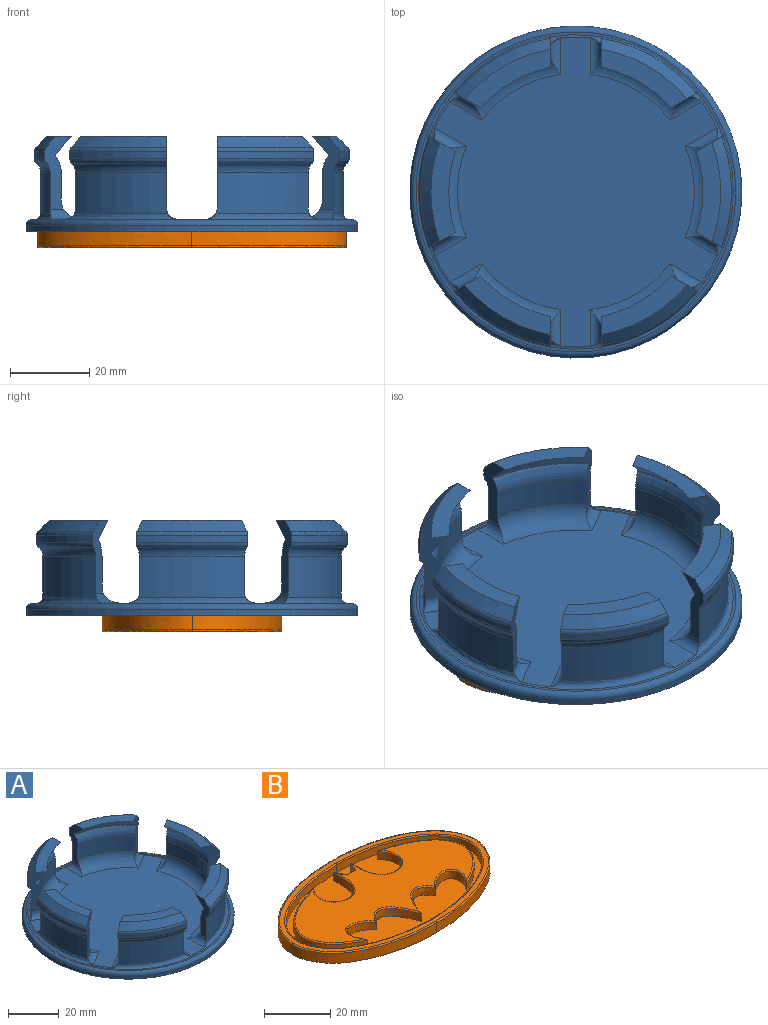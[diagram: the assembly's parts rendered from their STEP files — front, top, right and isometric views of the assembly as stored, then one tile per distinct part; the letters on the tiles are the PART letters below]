
ASSEMBLY  parts=2 mates=1
PART A: 102 faces, bbox 90.7x90.7x24.1 mm
  f0: cylinder r=38.1mm len=27.08mm, axis (0,0,-1), area 280.7mm2, adj f3,f66,f94,f96,f99,f101
  f1: cylinder r=39.69mm len=28.18mm, axis (0,0,-1), area 51mm2, adj f5,f6,f94,f99
  f2: plane 24.96x6.16mm, normal (0,0,1), area 103.8mm2, adj f4,f10,f94,f99
  f3: torus R=41.27mm, axis (0,0,1), area 74.2mm2, adj f0,f6,f94,f99
  f4: cone r=36.51mm half-angle=45deg, axis (0,0,-1), area 103.8mm2, adj f2,f5,f94,f99
  f5: torus R=38.16mm, axis (0,0,1), area 34.3mm2, adj f1,f4,f94,f99
  f6: torus R=38.16mm, axis (0,0,-1), area 36.9mm2, adj f1,f3,f94,f99
  f7: cylinder r=34.92mm len=23.34mm, axis (0,0,-1), area 158.2mm2, adj f9,f11,f94,f99
  f8: cylinder r=36.51mm len=24.96mm, axis (0,0,-1), area 10.4mm2, adj f9,f10,f94,f99
  f9: torus R=41.27mm, axis (0,0,1), area 112.2mm2, adj f7,f8,f94,f99
  f10: cone r=34.27mm half-angle=45deg, axis (0,0,-1), area 146.5mm2, adj f2,f8,f94,f99
  f11: torus R=29.84mm, axis (0,0,1), area 184.7mm2, adj f7,f72,f94,f96,f99,f101
  f12: cylinder r=38.1mm len=23.46mm, axis (0,0,-1), area 280.7mm2, adj f15,f66,f90,f92,f95,f97
  f13: cylinder r=39.69mm len=24.4mm, axis (0,0,-1), area 51mm2, adj f17,f18,f90,f95
  f14: plane 21.61x14.76mm, normal (0,0,1), area 103.8mm2, adj f16,f22,f90,f95
  f15: torus R=41.27mm, axis (0,0,1), area 74.2mm2, adj f12,f18,f90,f95
  f16: cone r=36.51mm half-angle=45deg, axis (0,0,-1), area 103.8mm2, adj f14,f17,f90,f95
  f17: torus R=38.16mm, axis (0,0,1), area 34.3mm2, adj f13,f16,f90,f95
  f18: torus R=38.16mm, axis (0,0,-1), area 36.9mm2, adj f13,f15,f90,f95
  f19: cylinder r=34.92mm len=20.22mm, axis (0,0,-1), area 158.2mm2, adj f21,f23,f90,f95
  f20: cylinder r=36.51mm len=21.61mm, axis (0,0,-1), area 10.4mm2, adj f21,f22,f90,f95
  f21: torus R=41.27mm, axis (0,0,1), area 112.2mm2, adj f19,f20,f90,f95
  f22: cone r=34.27mm half-angle=45deg, axis (0,0,-1), area 146.5mm2, adj f14,f20,f90,f95
  f23: torus R=29.84mm, axis (0,0,1), area 184.7mm2, adj f19,f72,f90,f92,f95,f97
  f24: cylinder r=38.1mm len=23.46mm, axis (0,0,-1), area 280.7mm2, adj f27,f66,f86,f88,f91,f93
  f25: cylinder r=39.69mm len=24.4mm, axis (0,0,-1), area 51mm2, adj f29,f30,f86,f91
  f26: plane 21.61x14.76mm, normal (0,0,1), area 103.8mm2, adj f28,f34,f86,f91
  f27: torus R=41.27mm, axis (0,0,1), area 74.2mm2, adj f24,f30,f86,f91
  f28: cone r=36.51mm half-angle=45deg, axis (0,0,-1), area 103.8mm2, adj f26,f29,f86,f91
  f29: torus R=38.16mm, axis (0,0,1), area 34.3mm2, adj f25,f28,f86,f91
  f30: torus R=38.16mm, axis (0,0,-1), area 36.9mm2, adj f25,f27,f86,f91
  f31: cylinder r=34.92mm len=20.22mm, axis (0,0,-1), area 158.2mm2, adj f33,f35,f86,f91
  f32: cylinder r=36.51mm len=21.61mm, axis (0,0,-1), area 10.4mm2, adj f33,f34,f86,f91
  f33: torus R=41.27mm, axis (0,0,1), area 112.2mm2, adj f31,f32,f86,f91
  f34: cone r=34.27mm half-angle=45deg, axis (0,0,-1), area 146.5mm2, adj f26,f32,f86,f91
  f35: torus R=29.84mm, axis (0,0,1), area 184.7mm2, adj f31,f72,f86,f88,f91,f93
  f36: cylinder r=38.1mm len=27.08mm, axis (0,0,-1), area 280.7mm2, adj f39,f66,f82,f84,f87,f89
  f37: cylinder r=39.69mm len=28.18mm, axis (0,0,-1), area 51mm2, adj f41,f42,f82,f87
  f38: plane 24.96x6.16mm, normal (0,0,1), area 103.8mm2, adj f40,f46,f82,f87
  f39: torus R=41.27mm, axis (0,0,1), area 74.2mm2, adj f36,f42,f82,f87
  f40: cone r=36.51mm half-angle=45deg, axis (0,0,-1), area 103.8mm2, adj f38,f41,f82,f87
  f41: torus R=38.16mm, axis (0,0,1), area 34.3mm2, adj f37,f40,f82,f87
  f42: torus R=38.16mm, axis (0,0,-1), area 36.9mm2, adj f37,f39,f82,f87
  f43: cylinder r=34.92mm len=23.34mm, axis (0,0,-1), area 158.2mm2, adj f45,f47,f82,f87
  f44: cylinder r=36.51mm len=24.96mm, axis (0,0,-1), area 10.4mm2, adj f45,f46,f82,f87
  f45: torus R=41.27mm, axis (0,0,1), area 112.2mm2, adj f43,f44,f82,f87
  f46: cone r=34.27mm half-angle=45deg, axis (0,0,-1), area 146.5mm2, adj f38,f44,f82,f87
  f47: torus R=29.84mm, axis (0,0,1), area 184.7mm2, adj f43,f72,f82,f84,f87,f89
  f48: cylinder r=38.1mm len=23.46mm, axis (0,0,-1), area 280.7mm2, adj f51,f66,f78,f80,f83,f85
  f49: cylinder r=39.69mm len=24.4mm, axis (0,0,-1), area 51mm2, adj f53,f54,f78,f83
  f50: plane 21.61x14.76mm, normal (0,0,1), area 103.8mm2, adj f52,f58,f78,f83
  f51: torus R=41.27mm, axis (0,0,1), area 74.2mm2, adj f48,f54,f78,f83
  f52: cone r=36.51mm half-angle=45deg, axis (0,0,-1), area 103.8mm2, adj f50,f53,f78,f83
  f53: torus R=38.16mm, axis (0,0,1), area 34.3mm2, adj f49,f52,f78,f83
  f54: torus R=38.16mm, axis (0,0,-1), area 36.9mm2, adj f49,f51,f78,f83
  f55: cylinder r=34.92mm len=20.22mm, axis (0,0,-1), area 158.2mm2, adj f57,f59,f78,f83
  f56: cylinder r=36.51mm len=21.61mm, axis (0,0,-1), area 10.4mm2, adj f57,f58,f78,f83
  f57: torus R=41.27mm, axis (0,0,1), area 112.2mm2, adj f55,f56,f78,f83
  f58: cone r=34.27mm half-angle=45deg, axis (0,0,-1), area 146.5mm2, adj f50,f56,f78,f83
  f59: torus R=29.84mm, axis (0,0,1), area 184.7mm2, adj f55,f72,f78,f80,f83,f85
  f60: cylinder r=41.85mm len=83.69mm, axis (0,0,-1), area 400.7mm2, adj f62,f67
  f61: plane 80.65x80.65mm, normal (0,0,1), area 175.4mm2, adj f66,f67
  f62: plane 83.69x83.69mm, normal (0,0,-1), area 5501.3mm2, adj f60
  f63: cylinder r=38.1mm len=23.46mm, axis (0,0,-1), area 280.7mm2, adj f66,f68,f79,f81,f98,f100
  f64: cylinder r=39.69mm len=24.4mm, axis (0,0,-1), area 51mm2, adj f70,f71,f79,f98
  f65: plane 21.61x14.76mm, normal (0,0,1), area 103.8mm2, adj f69,f76,f79,f98
  f66: torus R=39.62mm, axis (0,0,1), area 476.4mm2, adj f0,f12,f24,f36,f48,f61,f63,f72
  f67: torus R=40.32mm, axis (0,0,1), area 621.1mm2, adj f60,f61
  f68: torus R=41.27mm, axis (0,0,1), area 74.2mm2, adj f63,f71,f79,f98
  f69: cone r=36.51mm half-angle=45deg, axis (0,0,-1), area 103.8mm2, adj f65,f70,f79,f98
  f70: torus R=38.16mm, axis (0,0,1), area 34.3mm2, adj f64,f69,f79,f98
  f71: torus R=38.16mm, axis (0,0,-1), area 36.9mm2, adj f64,f68,f79,f98
  f72: plane 78.03x71.06mm, normal (0,0,1), area 3218.4mm2, adj f11,f23,f35,f47,f59,f66,f77,f80
  f73: cylinder r=34.92mm len=20.22mm, axis (0,0,-1), area 158.2mm2, adj f75,f77,f79,f98
  f74: cylinder r=36.51mm len=21.61mm, axis (0,0,-1), area 10.4mm2, adj f75,f76,f79,f98
  f75: torus R=41.27mm, axis (0,0,1), area 112.2mm2, adj f73,f74,f79,f98
  f76: cone r=34.27mm half-angle=45deg, axis (0,0,-1), area 146.5mm2, adj f65,f74,f79,f98
  f77: torus R=29.84mm, axis (0,0,1), area 184.7mm2, adj f72,f73,f79,f81,f98,f100
  f78: plane 18.42x7.92mm, normal (-1,0,0), area 66mm2, adj f48,f49,f50,f51,f52,f53,f54,f55
  f79: plane 18.42x7.92mm, normal (1,0,0), area 66mm2, adj f63,f64,f65,f68,f69,f70,f71,f73
  f80: cylinder r=2.54mm len=9.23mm, axis (0,-1,0), area 25.6mm2, adj f48,f59,f66,f72,f78
  f81: cylinder r=2.54mm len=9.23mm, axis (0,1,0), area 25.6mm2, adj f63,f66,f72,f77,f79
  f82: plane 18.42x6.88mm, normal (-0.5,0.87,0), area 66mm2, adj f36,f37,f38,f39,f40,f41,f42,f43
  f83: plane 18.42x6.88mm, normal (0.5,-0.87,0), area 66mm2, adj f48,f49,f50,f51,f52,f53,f54,f55
  f84: cylinder r=2.54mm len=9.26mm, axis (-0.87,-0.5,0), area 25.6mm2, adj f36,f47,f66,f72,f82
  f85: cylinder r=2.54mm len=9.26mm, axis (0.87,0.5,0), area 25.6mm2, adj f48,f59,f66,f72,f83
  f86: plane 18.42x6.88mm, normal (0.5,0.87,0), area 66mm2, adj f24,f25,f26,f27,f28,f29,f30,f31
  f87: plane 18.42x6.88mm, normal (-0.5,-0.87,0), area 66mm2, adj f36,f37,f38,f39,f40,f41,f42,f43
  f88: cylinder r=2.54mm len=9.26mm, axis (-0.87,0.5,0), area 25.6mm2, adj f24,f35,f66,f72,f86
  f89: cylinder r=2.54mm len=9.26mm, axis (0.87,-0.5,0), area 25.6mm2, adj f36,f47,f66,f72,f87
  f90: plane 18.42x7.92mm, normal (1,0,0), area 66mm2, adj f12,f13,f14,f15,f16,f17,f18,f19
  f91: plane 18.42x7.92mm, normal (-1,0,0), area 66mm2, adj f24,f25,f26,f27,f28,f29,f30,f31
  f92: cylinder r=2.54mm len=9.23mm, axis (0,1,0), area 25.6mm2, adj f12,f23,f66,f72,f90
  f93: cylinder r=2.54mm len=9.23mm, axis (0,-1,0), area 25.6mm2, adj f24,f35,f66,f72,f91
  f94: plane 18.42x6.88mm, normal (0.5,-0.87,0), area 66mm2, adj f0,f1,f2,f3,f4,f5,f6,f7
  f95: plane 18.42x6.88mm, normal (-0.5,0.87,0), area 66mm2, adj f12,f13,f14,f15,f16,f17,f18,f19
  f96: cylinder r=2.54mm len=9.26mm, axis (0.87,0.5,0), area 25.6mm2, adj f0,f11,f66,f72,f94
  f97: cylinder r=2.54mm len=9.26mm, axis (-0.87,-0.5,0), area 25.6mm2, adj f12,f23,f66,f72,f95
  f98: plane 18.42x6.88mm, normal (-0.5,-0.87,0), area 66mm2, adj f63,f64,f65,f68,f69,f70,f71,f73
  f99: plane 18.42x6.88mm, normal (0.5,0.87,0), area 66mm2, adj f0,f1,f2,f3,f4,f5,f6,f7
  f100: cylinder r=2.54mm len=9.26mm, axis (0.87,-0.5,0), area 25.6mm2, adj f63,f66,f72,f77,f98
  f101: cylinder r=2.54mm len=9.26mm, axis (-0.87,0.5,0), area 25.6mm2, adj f0,f11,f66,f72,f99
PART B: 44 faces, bbox 78.9x46x4 mm
  f0: plane 3.67x2.8mm, normal (-0.88,0.47,0), area 11.7mm2, adj f1,f11,f13,f34
  f1: extruded ~2.8x1.56mm, area 4.4mm2, adj f0,f2,f13,f32
  f2: extruded ~2.8x1.56mm, area 4.4mm2, adj f1,f3,f13,f30
  f3: plane 3.67x2.8mm, normal (0.88,0.47,0), area 11.7mm2, adj f2,f4,f13,f28
  f4: extruded ~12.62x12.54mm, area 88.2mm2, adj f3,f5,f13,f26
  f5: extruded ~30.53x20.42mm, area 134.8mm2, adj f4,f6,f13,f24
  f6: extruded ~10.44x8.51mm, area 54mm2, adj f5,f7,f13,f25
  f7: extruded ~12.69x10.07mm, area 55.3mm2, adj f6,f8,f13,f27
  f8: extruded ~12.69x10.07mm, area 55.3mm2, adj f7,f9,f13,f29
  f9: extruded ~10.44x8.51mm, area 54mm2, adj f8,f10,f13,f31
  f10: extruded ~30.53x20.42mm, area 134.8mm2, adj f9,f11,f13,f33
  f11: extruded ~12.62x12.54mm, area 88.2mm2, adj f0,f10,f13,f35
  f12: plane 67.48x31.08mm, normal (0,0,1), area 1146.8mm2, adj f24,f25,f26,f27,f28,f29,f30,f31
  f13: plane 73.37x40.47mm, normal (0,0,1), area 1081.9mm2, adj f0,f1,f2,f3,f4,f5,f6,f7
  f14: extruded ~38.97x22.74mm, area 178mm2, adj f15,f21,f23,f38
  f15: extruded ~38.97x22.52mm, area 177.1mm2, adj f14,f16,f23,f36
  f16: extruded ~38.97x22.52mm, area 177.1mm2, adj f15,f21,f23,f37
  f17: extruded ~36.58x20.23mm, area 127.5mm2, adj f13,f18,f20,f42
  f18: extruded ~36.58x20.23mm, area 127.5mm2, adj f13,f17,f19,f40
  f19: extruded ~36.58x20.23mm, area 127.6mm2, adj f13,f18,f20,f41
  f20: extruded ~36.58x20.23mm, area 127.6mm2, adj f13,f17,f19,f43
  f21: extruded ~38.97x22.74mm, area 178mm2, adj f14,f16,f23,f39
  f22: plane 77.18x44.48mm, normal (0,0,1), area 303.5mm2, adj f36,f37,f38,f39,f40,f41,f42,f43
  f23: plane 77.97x45.27mm, normal (0,0,-1), area 2781mm2, adj f14,f15,f16,f21
  f24: bspline ~31.26x22.28mm, area 29.3mm2, adj f5,f12,f25,f26
  f25: bspline ~11.36x11.31mm, area 11.8mm2, adj f6,f12,f24,f27
  f26: bspline ~18.54x13.53mm, area 19.3mm2, adj f4,f12,f24,f28
  f27: bspline ~13.61x10.84mm, area 12.1mm2, adj f7,f12,f25,f29
  f28: cylinder r=0.4mm len=4.1mm, axis (0.47,-0.88,0), area 2.2mm2, adj f3,f12,f26,f30
  f29: bspline ~13.61x10.84mm, area 12.1mm2, adj f8,f12,f27,f31
  f30: bspline ~3.06x0.64mm, area 1.1mm2, adj f2,f12,f28,f32
  f31: bspline ~11.36x11.31mm, area 11.8mm2, adj f9,f12,f29,f33
  f32: bspline ~3.06x0.64mm, area 1.1mm2, adj f1,f12,f30,f34
  f33: bspline ~31.11x21.99mm, area 29.3mm2, adj f10,f12,f31,f35
  f34: cylinder r=0.4mm len=4.1mm, axis (0.47,0.88,0), area 2.2mm2, adj f0,f12,f32,f35
  f35: bspline ~18.54x13.53mm, area 19.3mm2, adj f11,f12,f33,f34
  f36: bspline ~39.85x32.85mm, area 30.8mm2, adj f15,f22,f37,f38
  f37: bspline ~39.85x32.85mm, area 30.8mm2, adj f16,f22,f36,f39
  f38: bspline ~39.58x26.29mm, area 30.9mm2, adj f14,f22,f36,f39
  f39: bspline ~39.58x26.29mm, area 30.9mm2, adj f21,f22,f37,f38
  f40: bspline ~38.46x29.45mm, area 28.7mm2, adj f18,f22,f41,f42
  f41: bspline ~37.6x34.23mm, area 28.8mm2, adj f19,f22,f40,f43
  f42: bspline ~38.46x29.45mm, area 28.7mm2, adj f17,f22,f40,f43
  f43: bspline ~37.59x34.23mm, area 28.8mm2, adj f20,f22,f41,f42
PLACE A t=(-3.33,100.37,15.27)mm
PLACE B rot(axis=(1,0,0),180deg) t=(-43.4,130.46,15.27)mm
MATE planar B.f23 <-> A.f60  axis (0,0,1) through (-3.33,100.37,15.27)mm
